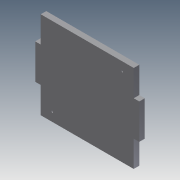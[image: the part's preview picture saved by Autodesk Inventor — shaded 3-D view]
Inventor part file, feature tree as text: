
AUTODESK INVENTOR PART (.ipt)
format: ipt  version: 2011 (Build 150239000, 239)  size: 137,216 bytes
history: native  units: in
note: dims shown in document units (in); Inventor stores cm internally (conversion verified against a paired STEP export)
features: extrude x6, sketch x6
ambient origin geometry x8: Origin, YZ Plane, XZ Plane, XY Plane, X Axis, Y Axis, Z Axis, Center Point
bodies: Solid1 (feature_tree)
feature tree (12):
  extrude  "Extrusion1"  Depth=1.9685in
  extrude  "Extrusion2"  Depth=0.375in TaperAngle=0.0deg
  extrude  "Extrusion3"  Depth=0.5906in
  extrude  "Extrusion4"  Depth=0.5906in
  extrude  "Extrusion5"  Depth=0.7874in
  extrude  "Extrusion6"  Depth=0.7874in
  sketch  "Sketch1"  dims[d0=1.9685in d1=1.9685in]
  sketch  "Sketch2"  dims[d2=0.125in d3=0.0in d4=0.375in d5=0.0in]
  sketch  "Sketch3"  dims[d6=0.125in d7=0.5906in]
  sketch  "Sketch4"  dims[d8=0.125in d9=0.5906in]
  sketch  "Sketch5"  dims[d10=0.375in d11=0.0in d12=0.7874in]
  sketch  "Sketch6"  dims[d13=0.1969in d14=0.7874in d15=0.1969in d16=0.0394in d17=0.0394in d18=1.0in d19=0.0in d20=0.0625in d21=0.0625in d22=1.0in d23=0.0in d24=0.125in d25=0.0in]
